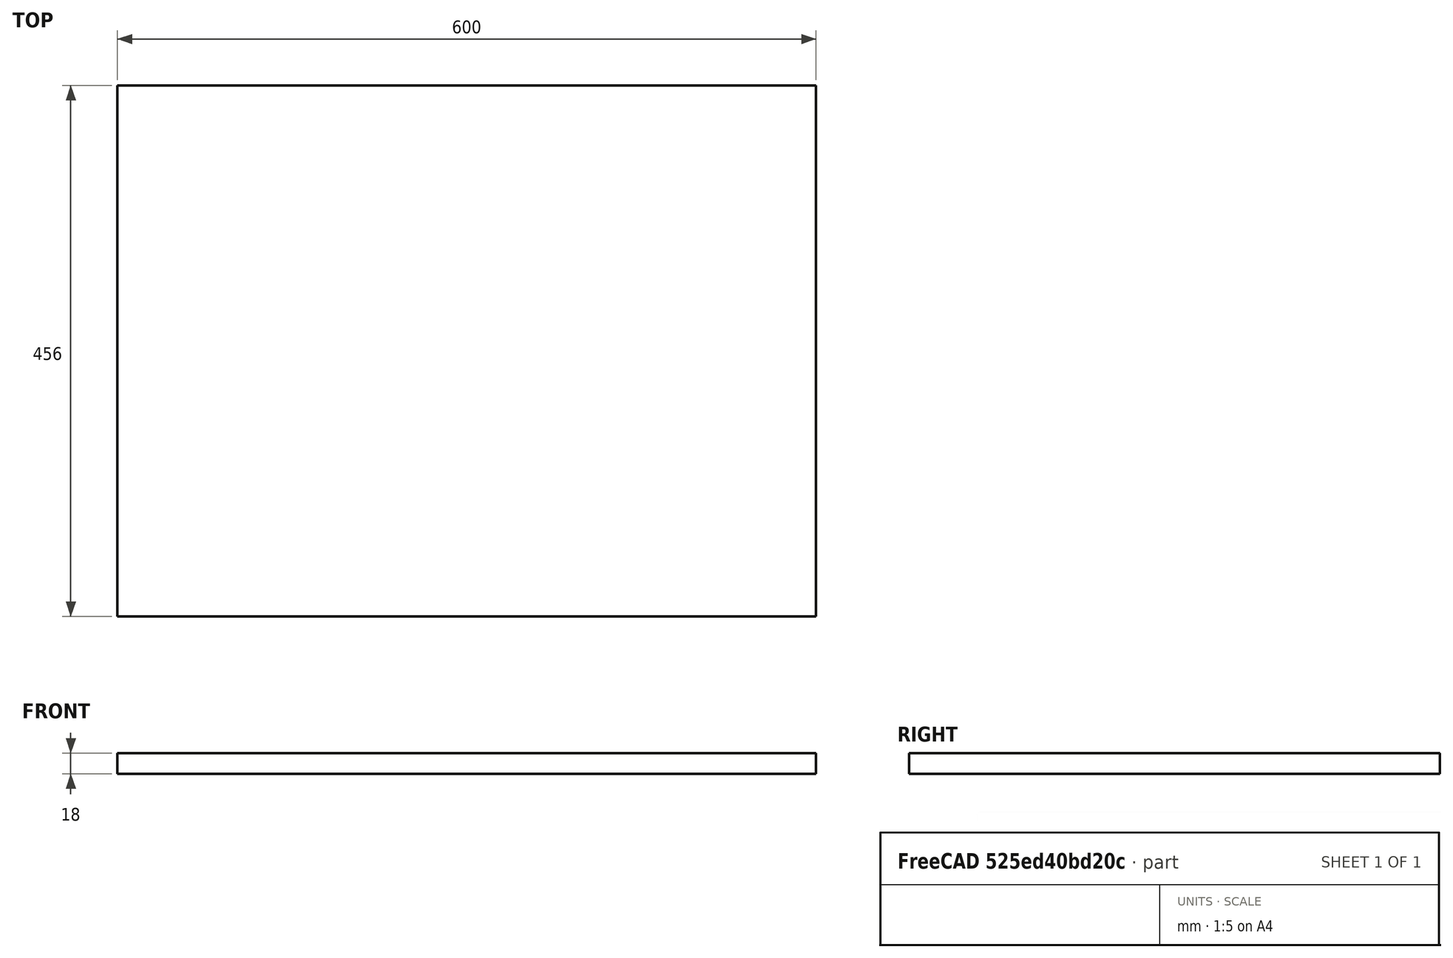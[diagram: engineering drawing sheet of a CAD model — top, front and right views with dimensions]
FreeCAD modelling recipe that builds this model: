
FCSTD DOCUMENT  (FreeCAD 0.18R4 (GitTag))
Label: bottom
License: All rights reserved
LicenseURL: http://en.wikipedia.org/wiki/All_rights_reserved
objects: Sketcher::SketchObject×1, PartDesign::Pad×1, PartDesign::Body×1
note: 4 computed .brp shape members not serialized (recipe doc carries the construction recipe); baked Part::Feature solids carry a one-line shape summary decoded from their .brp

FEATURE [Sketcher::SketchObject] Sketch
  MapMode = 5
  Support = -> [XY_Plane]
  sketch-geometry (4):
    g0: LineSegment StartX=0 StartY=0 StartZ=0 EndX=-600 EndY=0 EndZ=0
    g1: LineSegment StartX=-600 StartY=0 StartZ=0 EndX=-600 EndY=456 EndZ=0
    g2: LineSegment StartX=-600 StartY=456 StartZ=0 EndX=0 EndY=456 EndZ=0
    g3: LineSegment StartX=0 StartY=456 StartZ=0 EndX=0 EndY=0 EndZ=0
  constraints (11):
    c: Coincident(g0,g1)
    c: Coincident(g1,g2)
    c: Coincident(g2,g3)
    c: Coincident(g3,g0)
    c: Horizontal(g0)
    c: Horizontal(g2)
    c: Vertical(g1)
    c: Vertical(g3)
    c: Coincident(g0,g-1)
    c: DistanceY(g3,g3) = 456
    c: DistanceX(g0,g0) = 600
FEATURE [PartDesign::Pad] Pad
  Length = 18
  Length2 = 100
  Profile = -> Sketch
  Type = 0
FEATURE [PartDesign::Body] Body
  Group = -> [Sketch,Pad]
  Origin = -> Origin
  Tip = -> Pad
